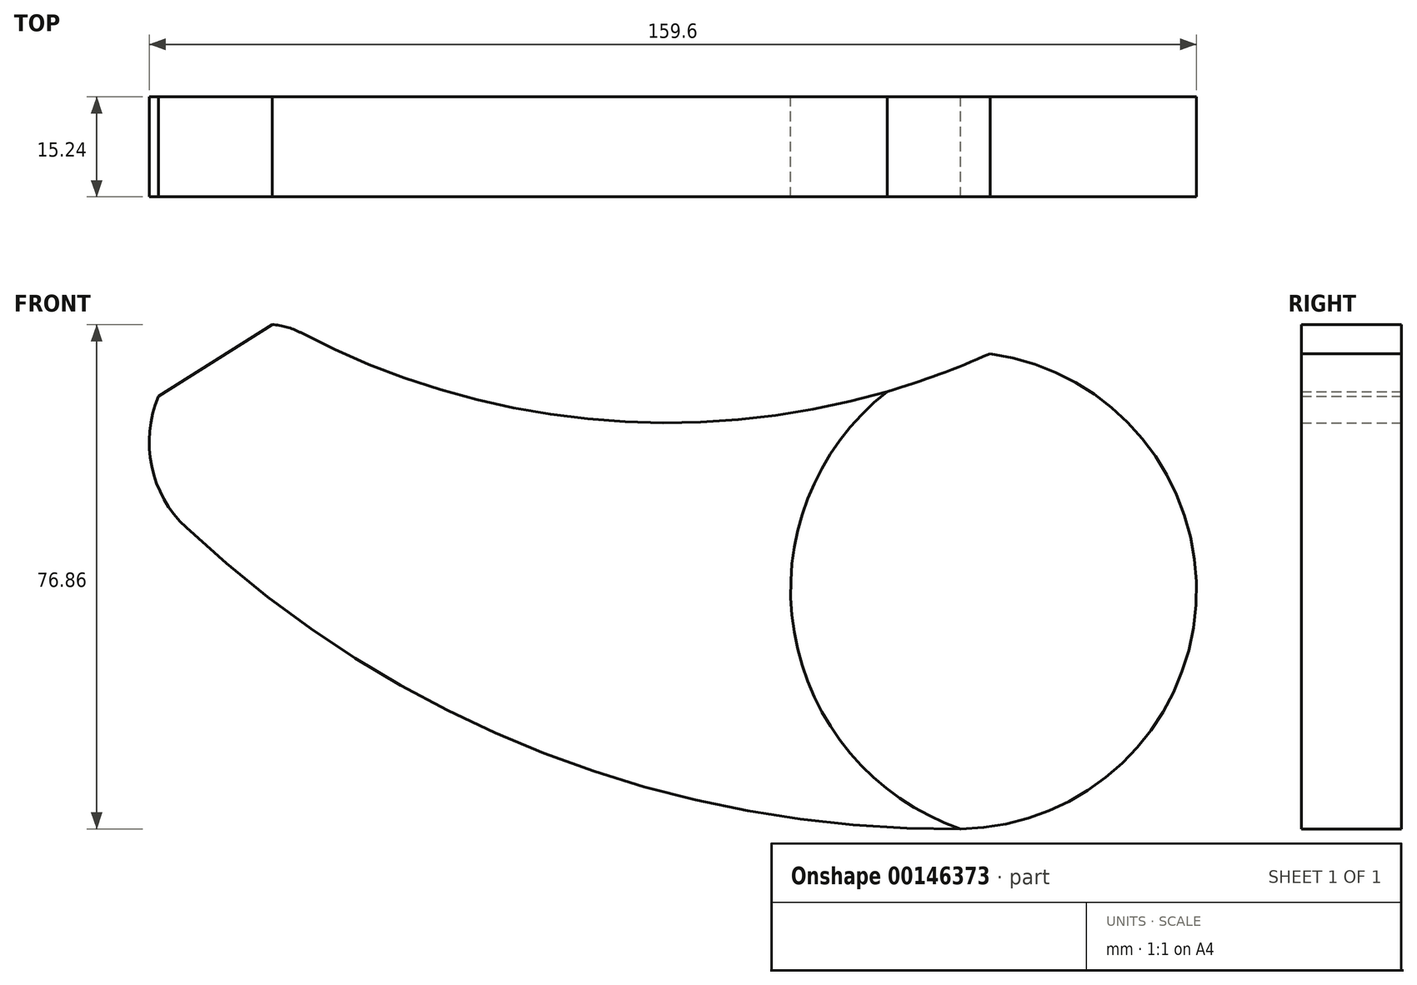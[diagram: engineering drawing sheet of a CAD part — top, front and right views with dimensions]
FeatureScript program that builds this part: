
annotation { "Feature Type Name" : "Feature", "Feature Type Description" : "" }
export const myFeature = defineFeature(function(context is Context, id is Id, definition is map)
    precondition{}
    {
        {
            var Q0;
            Q0=qCreatedBy(makeId("Front.planeOp"),FACE);
            var sketch = newSketch(context, id + "F0", { "sketchPlane" : qUnion([Q0])});
            skArc(sketch, "E0", {"start": v(-80.82, 25.9) * mm, "mid": v(-81.85, 15.21) * mm, "end": v(-76.59, 5.86) * mm});
            skArc(sketch, "E1", {"start": v(-76.59, 5.86) * mm, "mid": v(-22.04, -28.53) * mm, "end": v(41.4, -40.05) * mm});
            skArc(sketch, "E2", {"start": v(41.4, -40.05) * mm, "mid": v(77.3, -5.92) * mm, "end": v(45.9, 32.4) * mm});
            skArc(sketch, "E3", {"start": v(-59.24, 35.64) * mm, "mid": v(-7.04, 21.88) * mm, "end": v(45.9, 32.4) * mm});
            skPoint(sketch, "E4.visualSharp", {"position": v(-60.77, 36.46) * mm});
            skArc(sketch, "E4.filletArc", {"start": v(-59.24, 35.64) * mm, "mid": v(-61.3, 36.45) * mm, "end": v(-63.5, 36.8) * mm});
            skLineSegment(sketch, "E5", {"start": v(-63.5, 36.8) * mm, "end": v(-80.82, 25.9) * mm});
            skArc(sketch, "E6", {"start": v(30.24, 26.62) * mm, "mid": v(16.06, -10.03) * mm, "end": v(41.4, -40.05) * mm});
            skSolve(sketch);
        }
        {
            var Q0;
            Q0=makeQuery(id+"F0.imprint","IMPRINT",FACE,{"disambiguationData":[TD([[makeQuery(id+"F0.imprint","IMPRINT",EDGE,{"derivedFrom":sQuery(id+"F0.wireOp",EDGE,"E0")}),1.0]])]});
            extrude(context, id + "F1", {"entities" : qUnion([Q0]), "depth" : 15.24 * mm});
        }
        {
            var Q0;
            {var subQ0=sQuery(id+"F0.wireOp",EDGE,"E2");Q0=makeQuery(id+"F0.imprint","IMPRINT",FACE,{"disambiguationData":[TD([[makeQuery(id+"F0.imprint","IMPRINT",EDGE,{"derivedFrom":subQ0}),1.0]])]});}
            extrude(context, id + "F2", {"entities" : qUnion([Q0]), "depth" : 15.24 * mm});
        }
    });
